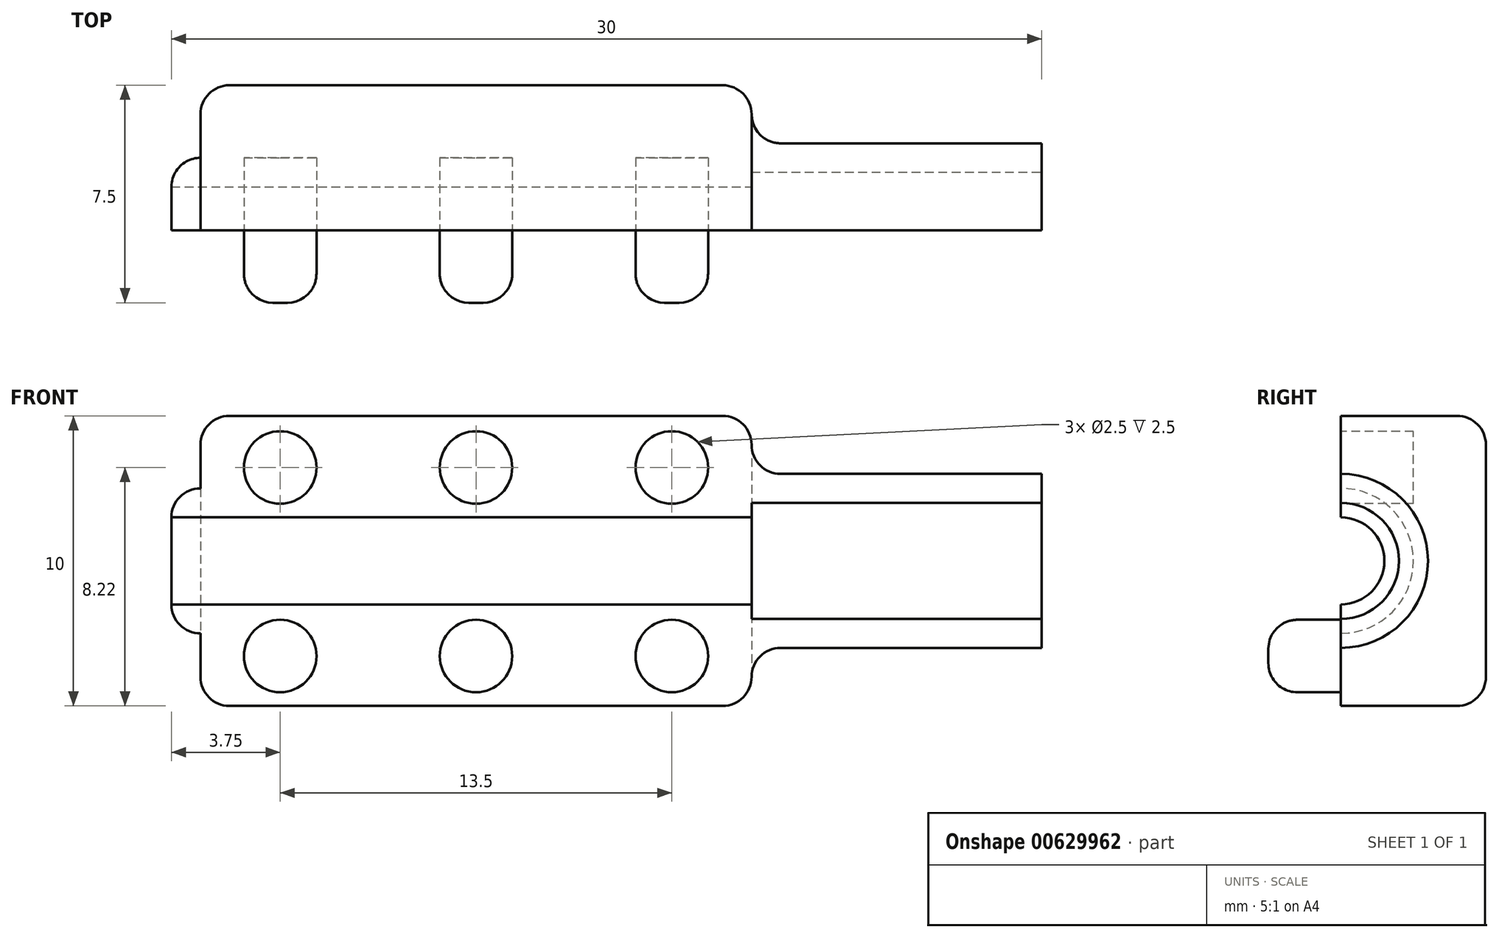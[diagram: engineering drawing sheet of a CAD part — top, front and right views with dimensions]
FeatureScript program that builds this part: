
annotation { "Feature Type Name" : "Feature", "Feature Type Description" : "" }
export const myFeature = defineFeature(function(context is Context, id is Id, definition is map)
    precondition{}
    {
        {
            var Q0;
            Q0=qCreatedBy(makeId("Front.planeOp"),FACE);
            var sketch = newSketch(context, id + "F0", { "sketchPlane" : qUnion([Q0])});
            skLineSegment(sketch, "E0.bottom", {"start": v(5, 2) * mm, "end": v(-5, 2) * mm});
            skLineSegment(sketch, "E0.top", {"start": v(5, 3) * mm, "end": v(-6, 3) * mm});
            skLineSegment(sketch, "E0.left", {"start": v(5, 2) * mm, "end": v(5, 3) * mm});
            skLineSegment(sketch, "E1.bottom", {"start": v(-6, 2.5) * mm, "end": v(-25, 2.5) * mm});
            skLineSegment(sketch, "E1.top", {"start": v(-5, 1.5) * mm, "end": v(-25, 1.5) * mm});
            skLineSegment(sketch, "E1.left", {"start": v(-5, 2) * mm, "end": v(-5, 1.5) * mm});
            skLineSegment(sketch, "E1.right", {"start": v(-25, 2.5) * mm, "end": v(-25, 1.5) * mm});
            skLineSegment(sketch, "E2", {"start": v(-6, 2.5) * mm, "end": v(-6, 3) * mm});
            skLineSegment(sketch, "E3", {"start": v(5, 0) * mm, "end": v(-25, 0) * mm});
            skPoint(sketch, "E4.end.orphan", {"position": v(0, 1.5) * mm});
            skPoint(sketch, "E5.orphan", {"position": v(-5, 2.5) * mm});
            skSolve(sketch);
        }
        {
            var Q0;
            Q0=makeQuery(id+"F0.imprint","IMPRINT",FACE,{"disambiguationData":[TD([[makeQuery(id+"F0.imprint","IMPRINT",EDGE,{"derivedFrom":sQuery(id+"F0.wireOp",EDGE,"E0.bottom")}),-1.0]])]});
            var Q1;
            Q1=sQuery(id+"F0.wireOp",EDGE,"E3");
            revolve(context, id + "F1", {"entities" : qUnion([Q0]), "axis" : qUnion([Q1]), "revolveType" : RevolveType.ONE_DIRECTION, "angle" : 180 * degree});
        }
        {
            var Q0;
            Q0=qCreatedBy(makeId("Front.planeOp"),FACE);
            var sketch = newSketch(context, id + "F2", { "sketchPlane" : qUnion([Q0])});
            skLineSegment(sketch, "E6.bottom", {"start": v(-24, 5) * mm, "end": v(-5, 5) * mm});
            skLineSegment(sketch, "E6.top", {"start": v(-24, -5) * mm, "end": v(-5, -5) * mm});
            skLineSegment(sketch, "E6.left", {"start": v(-24, 5) * mm, "end": v(-24, -5) * mm});
            skLineSegment(sketch, "E6.right", {"start": v(-5, 5) * mm, "end": v(-5, -5) * mm});
            skSolve(sketch);
        }
        {
            var Q0;
            Q0=makeQuery(id+"F2.imprint","IMPRINT",FACE,{"disambiguationData":[TD([[makeQuery(id+"F2.imprint","IMPRINT",EDGE,{"derivedFrom":sQuery(id+"F2.wireOp",EDGE,"E6.bottom")}),-1.0]])]});
            extrude(context, id + "F3", {"entities" : qUnion([Q0]), "operationType" : NewBodyOperationType.ADD, "oppositeDirection" : true, "depth" : 5 * mm, "offsetDistance" : 25 * mm});
        }
        {
            var Q0;
            Q0=qCreatedBy(makeId("Right.planeOp"),FACE);
            var sketch = newSketch(context, id + "F4", { "sketchPlane" : qUnion([Q0])});
            skCircle(sketch, "E7", {"center": v(0, 0) * mm, "radius": 1.5 * mm});
            skSolve(sketch);
        }
        {
            var Q0;
            Q0=makeQuery(id+"F4.imprint","IMPRINT",FACE,{"disambiguationData":[TD([[makeQuery(id+"F4.imprint","IMPRINT",EDGE,{"derivedFrom":sQuery(id+"F4.wireOp",EDGE,"E7")}),1.0]])]});
            extrude(context, id + "F5", {"entities" : qUnion([Q0]), "operationType" : NewBodyOperationType.REMOVE, "oppositeDirection" : true, "depth" : 25 * mm, "offsetDistance" : 25 * mm});
        }
        {
            var Q0;
            Q0=qCreatedBy(makeId("Front.planeOp"),FACE);
            var sketch = newSketch(context, id + "F6", { "sketchPlane" : qUnion([Q0])});
            skLineSegment(sketch, "E8.bottom", {"start": v(-5, 4.97) * mm, "end": v(-24, 4.97) * mm});
            skLineSegment(sketch, "E8.top", {"start": v(-5, -5.03) * mm, "end": v(-24, -5.03) * mm});
            skLineSegment(sketch, "E8.left", {"start": v(-5, 4.97) * mm, "end": v(-5, -5.03) * mm});
            skLineSegment(sketch, "E8.right", {"start": v(-24, 4.97) * mm, "end": v(-24, -5.03) * mm});
            skLineSegment(sketch, "E9", {"start": v(-5, 1.47) * mm, "end": v(-24, 1.47) * mm});
            skPoint(sketch, "E9.endSnap0", {"position": v(-24, -0.03) * mm});
            skLineSegment(sketch, "E10", {"start": v(-24, 1.47) * mm, "end": v(-24, -1.53) * mm});
            skLineSegment(sketch, "E11", {"start": v(-24, -1.53) * mm, "end": v(-5, -1.53) * mm});
            skLineSegment(sketch, "E12", {"start": v(-24, 3.22) * mm, "end": v(-24, -3.28) * mm});
            skCircle(sketch, "E13", {"center": v(-7.75, 3.22) * mm, "radius": 1.75 * mm});
            skCircle(sketch, "E14", {"center": v(-7.75, -3.28) * mm, "radius": 1.75 * mm});
            skCircle(sketch, "E15", {"center": v(-14.5, -3.28) * mm, "radius": 1.75 * mm});
            skCircle(sketch, "E16", {"center": v(-21.25, -3.28) * mm, "radius": 1.75 * mm});
            skCircle(sketch, "E17", {"center": v(-14.5, 3.22) * mm, "radius": 1.75 * mm});
            skCircle(sketch, "E18", {"center": v(-21.25, 3.22) * mm, "radius": 1.75 * mm});
            skCircle(sketch, "E19", {"center": v(-7.75, 3.22) * mm, "radius": 1.25 * mm});
            skCircle(sketch, "E20", {"center": v(-14.5, 3.22) * mm, "radius": 1.25 * mm});
            skCircle(sketch, "E21", {"center": v(-21.25, 3.22) * mm, "radius": 1.25 * mm});
            skCircle(sketch, "E22", {"center": v(-21.25, -3.28) * mm, "radius": 1.25 * mm});
            skCircle(sketch, "E23", {"center": v(-14.5, -3.28) * mm, "radius": 1.25 * mm});
            skCircle(sketch, "E24", {"center": v(-7.75, -3.28) * mm, "radius": 1.25 * mm});
            skSolve(sketch);
        }
        {
            var Q0;
            Q0=makeQuery(id+"F6.imprint","IMPRINT",FACE,{"disambiguationData":[TD([[makeQuery(id+"F6.imprint","IMPRINT",EDGE,{"derivedFrom":sQuery(id+"F6.wireOp",EDGE,"E21")}),1.0]])]});
            var Q1;
            Q1=makeQuery(id+"F6.imprint","IMPRINT",FACE,{"disambiguationData":[TD([[makeQuery(id+"F6.imprint","IMPRINT",EDGE,{"derivedFrom":sQuery(id+"F6.wireOp",EDGE,"E20")}),1.0]])]});
            var Q2;
            Q2=makeQuery(id+"F6.imprint","IMPRINT",FACE,{"disambiguationData":[TD([[makeQuery(id+"F6.imprint","IMPRINT",EDGE,{"derivedFrom":sQuery(id+"F6.wireOp",EDGE,"E19")}),1.0]])]});
            extrude(context, id + "F7", {"entities" : qUnion([Q0, Q1, Q2]), "operationType" : NewBodyOperationType.REMOVE, "oppositeDirection" : true, "depth" : 2.5 * mm, "offsetDistance" : 25 * mm});
        }
        {
            var Q0;
            Q0=makeQuery(id+"F6.imprint","IMPRINT",FACE,{"disambiguationData":[TD([[makeQuery(id+"F6.imprint","IMPRINT",EDGE,{"derivedFrom":sQuery(id+"F6.wireOp",EDGE,"E22")}),1.0]])]});
            var Q1;
            Q1=makeQuery(id+"F6.imprint","IMPRINT",FACE,{"disambiguationData":[TD([[makeQuery(id+"F6.imprint","IMPRINT",EDGE,{"derivedFrom":sQuery(id+"F6.wireOp",EDGE,"E23")}),1.0]])]});
            var Q2;
            Q2=makeQuery(id+"F6.imprint","IMPRINT",FACE,{"disambiguationData":[TD([[makeQuery(id+"F6.imprint","IMPRINT",EDGE,{"derivedFrom":sQuery(id+"F6.wireOp",EDGE,"E24")}),1.0]])]});
            extrude(context, id + "F8", {"entities" : qUnion([Q0, Q1, Q2]), "depth" : 2.5 * mm, "offsetDistance" : 25 * mm});
        }
        {
            var Q0;
            Q0=makeQuery(id+"F3.opExtrude","SWEPT_EDGE",EDGE,{"disambiguationData":[OSD([sQuery(id+"F2.wireOp",EDGE,"E6.bottom"),sQuery(id+"F2.wireOp",EDGE,"E6.right")])]});
            var Q1;
            Q1=makeQuery(id+"F3.opExtrude","CAP_EDGE",EDGE,{"disambiguationData":[OSD([sQuery(id+"F2.wireOp",EDGE,"E6.bottom")])],"isStart":false});
            var Q2;
            Q2=makeQuery(id+"F3.opExtrude","CAP_EDGE",EDGE,{"disambiguationData":[OSD([sQuery(id+"F2.wireOp",EDGE,"E6.right")])],"isStart":false});
            var Q3;
            Q3=makeQuery(id+"F3.opExtrude","CAP_EDGE",EDGE,{"disambiguationData":[OSD([sQuery(id+"F2.wireOp",EDGE,"E6.left")])],"isStart":false});
            var Q4;
            Q4=makeQuery(id+"F3.opExtrude","SWEPT_EDGE",EDGE,{"disambiguationData":[OSD([sQuery(id+"F2.wireOp",EDGE,"E6.bottom"),sQuery(id+"F2.wireOp",EDGE,"E6.left")])]});
            var Q5;
            Q5=makeQuery(id+"F3.opExtrude","SWEPT_EDGE",EDGE,{"disambiguationData":[OSD([sQuery(id+"F2.wireOp",EDGE,"E6.top"),sQuery(id+"F2.wireOp",EDGE,"E6.left")])]});
            var Q6;
            Q6=makeQuery(id+"F3.opExtrude","CAP_EDGE",EDGE,{"disambiguationData":[OSD([sQuery(id+"F2.wireOp",EDGE,"E6.top")])],"isStart":false});
            var Q7;
            Q7=makeQuery(id+"F3.opExtrude","SWEPT_EDGE",EDGE,{"disambiguationData":[OSD([sQuery(id+"F2.wireOp",EDGE,"E6.top"),sQuery(id+"F2.wireOp",EDGE,"E6.right")])]});
            var Q8;
            Q8=makeQuery(id+"F3.boolean.opBoolean","INTERSECT",EDGE,{"derivedFrom":[makeQuery(id+"F1.opRevolve","SWEPT_FACE",FACE,{"disambiguationData":[OSD([sQuery(id+"F0.wireOp",EDGE,"E0.top")])]}),makeQuery(id+"F3.opExtrude","SWEPT_FACE",FACE,{"disambiguationData":[OSD([sQuery(id+"F2.wireOp",EDGE,"E6.right")])]})]});
            fillet(context, id + "F9", {"entities" : qUnion([Q0, Q1, Q2, Q3, Q4, Q5, Q6, Q7, Q8]), "radius" : 1 * mm, "tangentPropagation" : true, "allowEdgeOverflow" : false});
        }
        {
            var Q0;
            Q0=makeQuery(id+"F1.opRevolve","SWEPT_EDGE",EDGE,{"disambiguationData":[OSD([sQuery(id+"F0.wireOp",EDGE,"E1.bottom"),sQuery(id+"F0.wireOp",EDGE,"E1.right")])]});
            fillet(context, id + "F10", {"entities" : qUnion([Q0]), "radius" : 1 * mm, "tangentPropagation" : true, "allowEdgeOverflow" : false});
        }
        {
            var Q0;
            Q0=makeQuery(id+"F8.opExtrude","CAP_EDGE",EDGE,{"disambiguationData":[OSD([sQuery(id+"F6.wireOp",EDGE,"E22")])],"isStart":false});
            var Q1;
            Q1=makeQuery(id+"F8.opExtrude","CAP_EDGE",EDGE,{"disambiguationData":[OSD([sQuery(id+"F6.wireOp",EDGE,"E23")])],"isStart":false});
            var Q2;
            Q2=makeQuery(id+"F8.opExtrude","CAP_EDGE",EDGE,{"disambiguationData":[OSD([sQuery(id+"F6.wireOp",EDGE,"E24")])],"isStart":false});
            fillet(context, id + "F11", {"entities" : qUnion([Q0, Q1, Q2]), "radius" : 1 * mm, "tangentPropagation" : true, "allowEdgeOverflow" : false});
        }
    });
